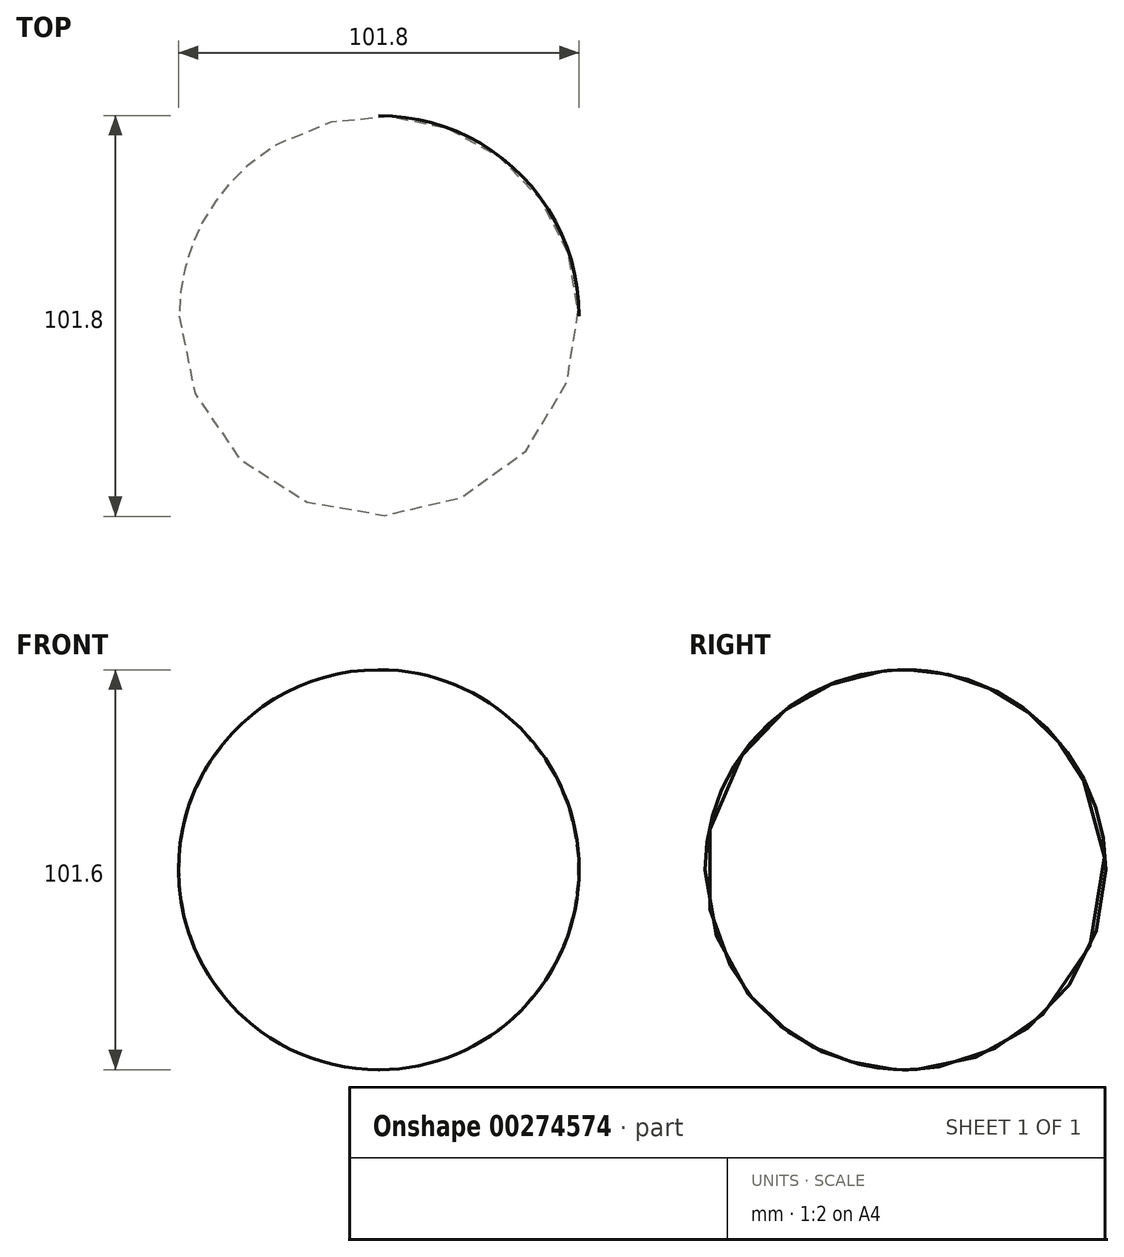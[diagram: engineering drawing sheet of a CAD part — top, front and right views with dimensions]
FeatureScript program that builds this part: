
annotation { "Feature Type Name" : "Feature", "Feature Type Description" : "" }
export const myFeature = defineFeature(function(context is Context, id is Id, definition is map)
    precondition{}
    {
        {
            var Q0;
            Q0=qCreatedBy(makeId("Front.planeOp"),FACE);
            var sketch = newSketch(context, id + "F0", { "sketchPlane" : qUnion([Q0])});
            skArc(sketch, "E0", {"start": v(-0.2, 50.8) * mm, "mid": v(-50.8, -0.1) * mm, "end": v(0, -50.8) * mm});
            skLineSegment(sketch, "E1", {"start": v(-0.2, 50.8) * mm, "end": v(0, -50.8) * mm});
            skSolve(sketch);
        }
        {
            var Q0;
            Q0 = qSketchRegion(id + "F0", true);
            var Q1;
            Q1=sQuery(id+"F0.wireOp",EDGE,"E1");
            revolve(context, id + "F1", {"entities" : qUnion([Q0]), "axis" : qUnion([Q1]), "revolveType" : RevolveType.FULL});
        }
    });
